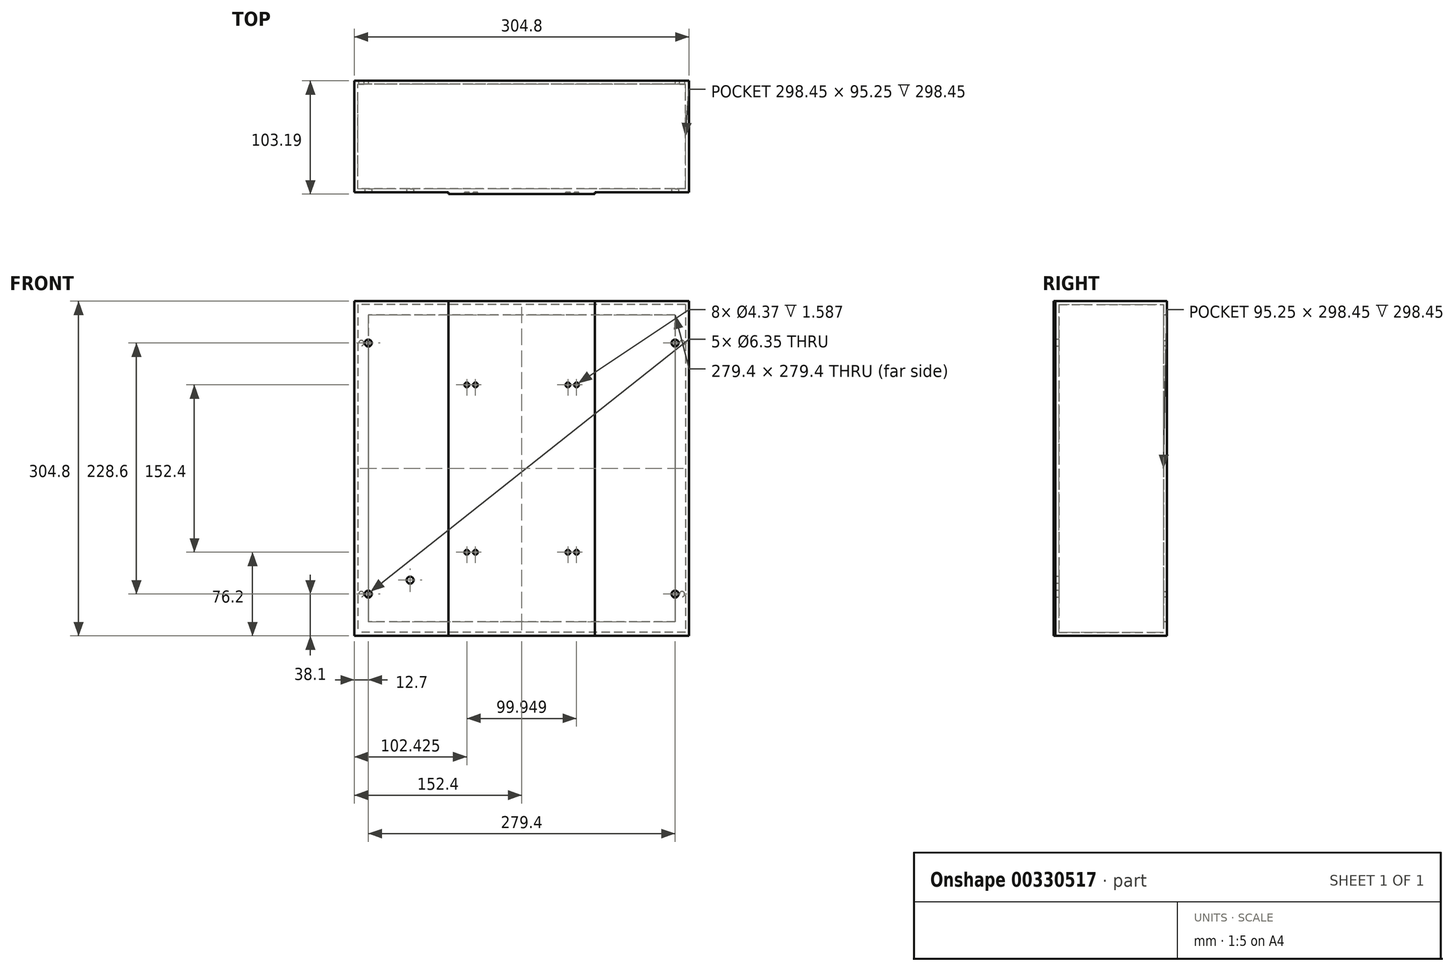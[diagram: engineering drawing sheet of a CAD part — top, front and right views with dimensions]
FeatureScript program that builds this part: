
annotation { "Feature Type Name" : "Feature", "Feature Type Description" : "" }
export const myFeature = defineFeature(function(context is Context, id is Id, definition is map)
    precondition{}
    {
        {
            var Q0;
            Q0=qCreatedBy(makeId("Front.planeOp"),FACE);
            var sketch = newSketch(context, id + "F0", { "sketchPlane" : qUnion([Q0])});
            skLineSegment(sketch, "E0.bottom", {"start": v(-66.67, 152.4) * mm, "end": v(66.68, 152.4) * mm});
            skLineSegment(sketch, "E0.top", {"start": v(-66.68, -152.4) * mm, "end": v(66.67, -152.4) * mm});
            skLineSegment(sketch, "E0.left", {"start": v(-66.67, 152.4) * mm, "end": v(-66.68, -152.4) * mm});
            skLineSegment(sketch, "E0.right", {"start": v(66.68, 152.4) * mm, "end": v(66.67, -152.4) * mm});
            skPoint(sketch, "E0.middle", {"position": v(0, 0) * mm});
            skLineSegment(sketch, "E1.bottom", {"start": v(42.1, 76.2) * mm, "end": v(-42.1, 76.2) * mm, "construction": true});
            skLineSegment(sketch, "E1.top", {"start": v(42.1, -76.2) * mm, "end": v(-42.1, -76.2) * mm, "construction": true});
            skLineSegment(sketch, "E1.left", {"start": v(42.1, 76.2) * mm, "end": v(42.1, -76.2) * mm, "construction": true});
            skLineSegment(sketch, "E1.right", {"start": v(-42.1, 76.2) * mm, "end": v(-42.1, -76.2) * mm, "construction": true});
            skLineSegment(sketch, "E2.bottom", {"start": v(49.97, 76.2) * mm, "end": v(-49.97, 76.2) * mm, "construction": true});
            skLineSegment(sketch, "E2.top", {"start": v(49.97, -76.2) * mm, "end": v(-49.97, -76.2) * mm, "construction": true});
            skLineSegment(sketch, "E2.left", {"start": v(49.97, 76.2) * mm, "end": v(49.97, -76.2) * mm, "construction": true});
            skLineSegment(sketch, "E2.right", {"start": v(-49.97, 76.2) * mm, "end": v(-49.97, -76.2) * mm, "construction": true});
            skCircle(sketch, "E3", {"center": v(-49.97, 76.2) * mm, "radius": 2.18 * mm});
            skCircle(sketch, "E4", {"center": v(-42.1, 76.2) * mm, "radius": 2.18 * mm});
            skCircle(sketch, "E5", {"center": v(42.1, 76.2) * mm, "radius": 2.18 * mm});
            skCircle(sketch, "E6", {"center": v(49.97, 76.2) * mm, "radius": 2.18 * mm});
            skCircle(sketch, "E7", {"center": v(-49.97, -76.2) * mm, "radius": 2.18 * mm});
            skCircle(sketch, "E8", {"center": v(-42.1, -76.2) * mm, "radius": 2.18 * mm});
            skCircle(sketch, "E9", {"center": v(42.1, -76.2) * mm, "radius": 2.18 * mm});
            skCircle(sketch, "E10", {"center": v(49.97, -76.2) * mm, "radius": 2.18 * mm});
            skSolve(sketch);
        }
        {
            var Q0;
            Q0=makeQuery(id+"F0.imprint","IMPRINT",FACE,{"disambiguationData":[TD([[makeQuery(id+"F0.imprint","IMPRINT",EDGE,{"derivedFrom":sQuery(id+"F0.wireOp",EDGE,"E0.bottom")}),-1.0]])]});
            extrude(context, id + "F1", {"entities" : qUnion([Q0]), "depth" : 1.59 * mm});
        }
        {
            var Q0;
            Q0=qCreatedBy(makeId("Front.planeOp"),FACE);
            var sketch = newSketch(context, id + "F2", { "sketchPlane" : qUnion([Q0])});
            skLineSegment(sketch, "E11.bottom", {"start": v(152.4, 152.4) * mm, "end": v(-152.4, 152.4) * mm});
            skLineSegment(sketch, "E11.top", {"start": v(152.4, -152.4) * mm, "end": v(-152.4, -152.4) * mm});
            skLineSegment(sketch, "E11.left", {"start": v(152.4, 152.4) * mm, "end": v(152.4, -152.4) * mm});
            skLineSegment(sketch, "E11.right", {"start": v(-152.4, 152.4) * mm, "end": v(-152.4, -152.4) * mm});
            skPoint(sketch, "E11.middle", {"position": v(0, 0) * mm});
            skCircle(sketch, "E12", {"center": v(-101.6, -101.6) * mm, "radius": 3.18 * mm});
            skCircle(sketch, "E13", {"center": v(-139.7, 114.3) * mm, "radius": 3.18 * mm});
            skCircle(sketch, "E14", {"center": v(-139.7, -114.3) * mm, "radius": 3.18 * mm});
            skCircle(sketch, "E15", {"center": v(139.7, -114.3) * mm, "radius": 3.18 * mm});
            skCircle(sketch, "E16", {"center": v(139.7, 114.3) * mm, "radius": 3.18 * mm});
            skSolve(sketch);
        }
        {
            var Q0;
            Q0=makeQuery(id+"F2.imprint","IMPRINT",FACE,{"disambiguationData":[TD([[makeQuery(id+"F2.imprint","IMPRINT",EDGE,{"derivedFrom":sQuery(id+"F2.wireOp",EDGE,"E11.bottom")}),1.0]])]});
            extrude(context, id + "F3", {"entities" : qUnion([Q0]), "operationType" : NewBodyOperationType.ADD, "oppositeDirection" : true, "depth" : 98.42 * mm});
        }
        {
            var Q0;
            Q0=makeQuery(id+"F3.opExtrude","CAP_FACE",FACE,{"disambiguationData":[OSD([sQuery(id+"F2.wireOp",EDGE,"E11.bottom"),sQuery(id+"F2.wireOp",EDGE,"E11.top"),sQuery(id+"F2.wireOp",EDGE,"E11.left"),sQuery(id+"F2.wireOp",EDGE,"E11.right"),sQuery(id+"F2.wireOp",EDGE,"E12"),sQuery(id+"F2.wireOp",EDGE,"E13"),sQuery(id+"F2.wireOp",EDGE,"E14"),sQuery(id+"F2.wireOp",EDGE,"E15"),sQuery(id+"F2.wireOp",EDGE,"E16")])],"isStart":false});
            var sketch = newSketch(context, id + "F4", { "sketchPlane" : qUnion([Q0])});
            skLineSegment(sketch, "E17.0", {"start": v(-149.22, -149.22) * mm, "end": v(149.22, -149.22) * mm});
            skLineSegment(sketch, "E17.1", {"start": v(-149.22, 149.23) * mm, "end": v(-149.22, -149.22) * mm});
            skLineSegment(sketch, "E17.2", {"start": v(-149.22, 149.23) * mm, "end": v(149.23, 149.23) * mm});
            skLineSegment(sketch, "E17.3", {"start": v(149.23, 149.23) * mm, "end": v(149.23, -149.22) * mm});
            skSolve(sketch);
        }
        {
            var Q0;
            Q0 = qSketchRegion(id + "F4", true);
            extrude(context, id + "F5", {"entities" : qUnion([Q0]), "operationType" : NewBodyOperationType.REMOVE, "oppositeDirection" : true, "depth" : 95.25 * mm});
        }
        {
            var Q0;
            Q0=makeQuery(id+"F3.opExtrude","CAP_FACE",FACE,{"disambiguationData":[OSD([sQuery(id+"F2.wireOp",EDGE,"E11.bottom"),sQuery(id+"F2.wireOp",EDGE,"E11.top"),sQuery(id+"F2.wireOp",EDGE,"E11.left"),sQuery(id+"F2.wireOp",EDGE,"E11.right"),sQuery(id+"F2.wireOp",EDGE,"E12"),sQuery(id+"F2.wireOp",EDGE,"E13"),sQuery(id+"F2.wireOp",EDGE,"E14"),sQuery(id+"F2.wireOp",EDGE,"E15"),sQuery(id+"F2.wireOp",EDGE,"E16")])],"isStart":false});
            var sketch = newSketch(context, id + "F6", { "sketchPlane" : qUnion([Q0])});
            skLineSegment(sketch, "E18.0", {"start": v(-152.4, -152.4) * mm, "end": v(152.4, -152.4) * mm});
            skLineSegment(sketch, "E19.0", {"start": v(152.4, 152.4) * mm, "end": v(152.4, -152.4) * mm});
            skLineSegment(sketch, "E20.0", {"start": v(-152.4, 152.4) * mm, "end": v(-152.4, -152.4) * mm});
            skLineSegment(sketch, "E21.0", {"start": v(-152.4, 152.4) * mm, "end": v(152.4, 152.4) * mm});
            skLineSegment(sketch, "E22.0", {"start": v(-139.7, -139.7) * mm, "end": v(139.7, -139.7) * mm});
            skLineSegment(sketch, "E22.1", {"start": v(-139.7, 139.7) * mm, "end": v(-139.7, -139.7) * mm});
            skLineSegment(sketch, "E22.2", {"start": v(-139.7, 139.7) * mm, "end": v(139.7, 139.7) * mm});
            skLineSegment(sketch, "E22.3", {"start": v(139.7, 139.7) * mm, "end": v(139.7, -139.7) * mm});
            skSolve(sketch);
        }
        {
            var Q0;
            Q0 = qSketchRegion(id + "F6", true);
            extrude(context, id + "F7", {"entities" : qUnion([Q0]), "operationType" : NewBodyOperationType.ADD, "depth" : 3.17 * mm});
        }
        {
            var Q0;
            Q0=makeQuery(id+"F7.opExtrude","CAP_FACE",FACE,{"disambiguationData":[OSD([sQuery(id+"F6.wireOp",EDGE,"E18.0"),sQuery(id+"F6.wireOp",EDGE,"E19.0"),sQuery(id+"F6.wireOp",EDGE,"E20.0"),sQuery(id+"F6.wireOp",EDGE,"E21.0"),sQuery(id+"F6.wireOp",EDGE,"E22.0"),sQuery(id+"F6.wireOp",EDGE,"E22.1"),sQuery(id+"F6.wireOp",EDGE,"E22.2"),sQuery(id+"F6.wireOp",EDGE,"E22.3")])],"isStart":false});
            var sketch = newSketch(context, id + "F8", { "sketchPlane" : qUnion([Q0])});
            skLineSegment(sketch, "E23", {"start": v(-139.7, 139.7) * mm, "end": v(-152.4, 139.7) * mm, "construction": true});
            skLineSegment(sketch, "E24", {"start": v(139.7, 139.7) * mm, "end": v(152.4, 139.7) * mm, "construction": true});
            skCircle(sketch, "E25.0", {"center": v(-139.7, 114.3) * mm, "radius": 3.18 * mm, "construction": true});
            skCircle(sketch, "E26.0", {"center": v(139.7, 114.3) * mm, "radius": 3.18 * mm, "construction": true});
            skCircle(sketch, "E27.0", {"center": v(139.7, -114.3) * mm, "radius": 3.18 * mm, "construction": true});
            skCircle(sketch, "E28.0", {"center": v(-139.7, -114.3) * mm, "radius": 3.18 * mm, "construction": true});
            skPoint(sketch, "E29", {"position": v(-146.05, 139.7) * mm});
            skPoint(sketch, "E30", {"position": v(146.05, 139.7) * mm});
            skCircle(sketch, "E31", {"center": v(-146.05, 114.3) * mm, "radius": 2.38 * mm});
            skCircle(sketch, "E32", {"center": v(146.05, 114.3) * mm, "radius": 2.38 * mm});
            skCircle(sketch, "E33", {"center": v(146.05, -114.3) * mm, "radius": 2.38 * mm});
            skCircle(sketch, "E34", {"center": v(-146.05, -114.3) * mm, "radius": 2.38 * mm});
            skSolve(sketch);
        }
        {
            var Q0;
            Q0 = qSketchRegion(id + "F8", true);
            extrude(context, id + "F9", {"entities" : qUnion([Q0]), "operationType" : NewBodyOperationType.REMOVE, "oppositeDirection" : true, "depth" : 25.4 * mm});
        }
        {
            var Q0;
            Q0=makeQuery(id+"F5.boolean.opBoolean","COPY",FACE,{"derivedFrom":makeQuery(id+"F5.opExtrude","CAP_FACE",FACE,{"disambiguationData":[OSD([sQuery(id+"F4.wireOp",EDGE,"E17.0"),sQuery(id+"F4.wireOp",EDGE,"E17.1"),sQuery(id+"F4.wireOp",EDGE,"E17.2"),sQuery(id+"F4.wireOp",EDGE,"E17.3")])],"isStart":false})});
            var sketch = newSketch(context, id + "F10", { "sketchPlane" : qUnion([Q0])});
            skLineSegment(sketch, "E35", {"start": v(-49.74, 34) * mm, "end": v(-76.46, 42.44) * mm});
            skLineSegment(sketch, "E36", {"start": v(49.74, 37.2) * mm, "end": v(31.67, 55.72) * mm});
            skLineSegment(sketch, "E37.bottom", {"start": v(-49.74, 0) * mm, "end": v(49.74, 0) * mm});
            skLineSegment(sketch, "E37.top", {"start": v(-49.74, -35.66) * mm, "end": v(49.74, -35.66) * mm});
            skLineSegment(sketch, "E37.left", {"start": v(-49.74, 0) * mm, "end": v(-49.74, -35.66) * mm});
            skLineSegment(sketch, "E37.right", {"start": v(49.74, 0) * mm, "end": v(49.74, -35.66) * mm});
            skSolve(sketch);
        }
    });
